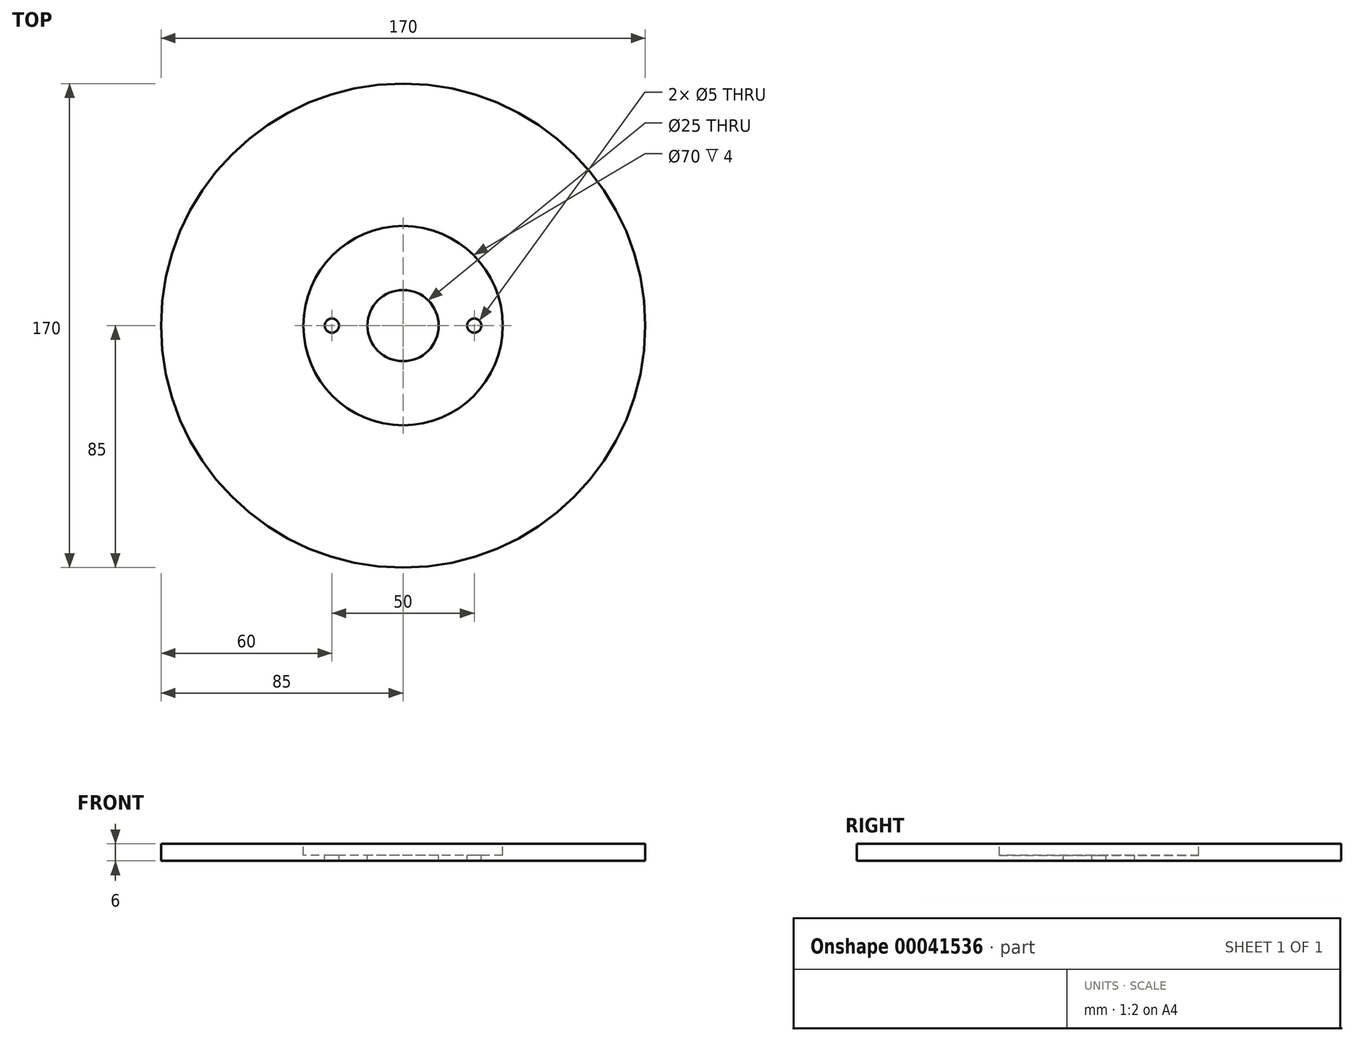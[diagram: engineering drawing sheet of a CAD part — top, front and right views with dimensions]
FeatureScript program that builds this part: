
annotation { "Feature Type Name" : "Feature", "Feature Type Description" : "" }
export const myFeature = defineFeature(function(context is Context, id is Id, definition is map)
    precondition{}
    {
        {
            var Q0;
            Q0=qCreatedBy(makeId("Top.planeOp"),FACE);
            var sketch = newSketch(context, id + "F0", { "sketchPlane" : qUnion([Q0])});
            skCircle(sketch, "E0", {"center": v(0, 0) * mm, "radius": 85 * mm});
            skSolve(sketch);
        }
        {
            var Q0;
            Q0=makeQuery(id+"F0.imprint","IMPRINT",FACE,{"disambiguationData":[TD([[makeQuery(id+"F0.imprint","IMPRINT",EDGE,{"derivedFrom":sQuery(id+"F0.wireOp",EDGE,"E0")}),1.0]])]});
            extrude(context, id + "F1", {"entities" : qUnion([Q0]), "depth" : 6 * mm});
        }
        {
            var Q0;
            Q0=makeQuery(id+"F1.opExtrude","CAP_FACE",FACE,{"disambiguationData":[OSD([sQuery(id+"F0.wireOp",EDGE,"E0")])],"isStart":false});
            var sketch = newSketch(context, id + "F2", { "sketchPlane" : qUnion([Q0])});
            skCircle(sketch, "E1", {"center": v(0, 0) * mm, "radius": 35 * mm});
            skCircle(sketch, "E2", {"center": v(0, 0) * mm, "radius": 12.5 * mm});
            skLineSegment(sketch, "E3", {"start": v(-46.38, 0) * mm, "end": v(60.64, 0) * mm, "construction": true});
            skPoint(sketch, "E4", {"position": v(-25, 0) * mm});
            skPoint(sketch, "E5", {"position": v(25, 0) * mm});
            skSolve(sketch);
        }
        {
            var Q0;
            Q0=sQuery(id+"F2.wireOp",VERTEX,"E4");
            var Q1;
            Q1=sQuery(id+"F2.wireOp",VERTEX,"E5");
            var Q2;
            Q2=makeQuery(id+"F1.opExtrude","SWEPT_BODY",BODY,{"disambiguationData":[OSD([sQuery(id+"F0.wireOp",EDGE,"E0")])]});
            hole(context, id + "F3", {"style" : HoleStyle.SIMPLE, "endStyle" : HoleEndStyle.THROUGH, "holeDiameter" : 5 * mm, "isTappedThrough" : true, "tappedDepth" : 12 * mm, "tapClearance" : 3, "locations" : qUnion([Q0, Q1]), "scope" : qUnion([Q2])});
        }
        {
            var Q0;
            Q0=makeQuery(id+"F2.imprint","IMPRINT",FACE,{"disambiguationData":[TD([[makeQuery(id+"F2.imprint","IMPRINT",EDGE,{"derivedFrom":sQuery(id+"F2.wireOp",EDGE,"E2")}),1.0]])]});
            extrude(context, id + "F4", {"entities" : qUnion([Q0]), "operationType" : NewBodyOperationType.REMOVE, "endBound" : BoundingType.THROUGH_ALL, "oppositeDirection" : true, "depth" : 25 * mm});
        }
        {
            var Q0;
            Q0=makeQuery(id+"F2.imprint","IMPRINT",FACE,{"disambiguationData":[TD([[makeQuery(id+"F2.imprint","IMPRINT",EDGE,{"derivedFrom":sQuery(id+"F2.wireOp",EDGE,"E1")}),1.0]])]});
            extrude(context, id + "F5", {"entities" : qUnion([Q0]), "operationType" : NewBodyOperationType.REMOVE, "oppositeDirection" : true, "depth" : 4 * mm});
        }
    });
